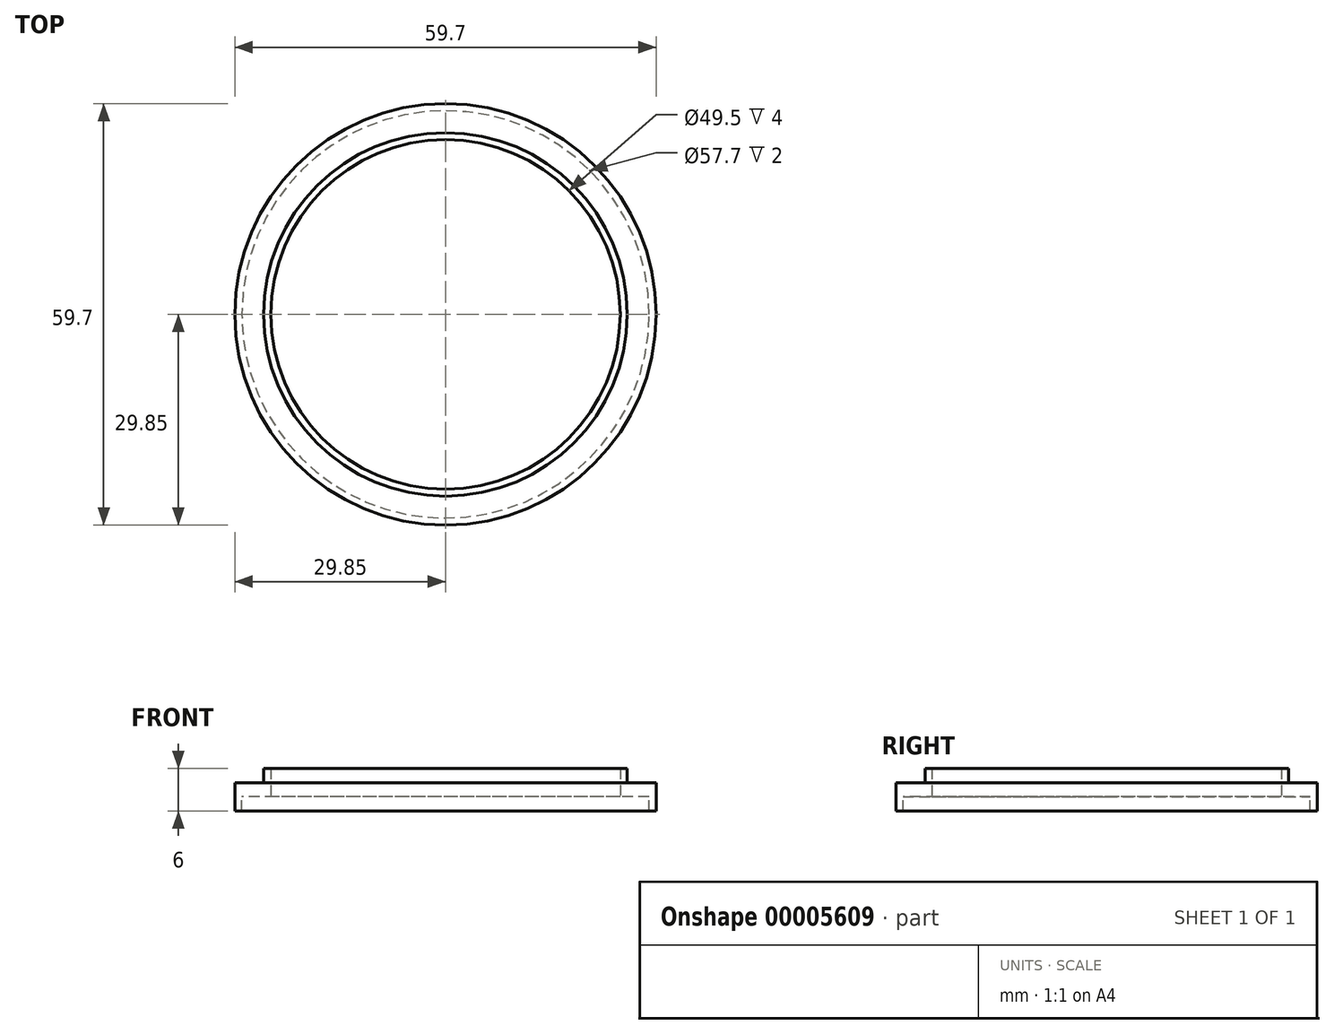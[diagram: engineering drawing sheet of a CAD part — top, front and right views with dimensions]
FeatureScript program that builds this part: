
annotation { "Feature Type Name" : "Feature", "Feature Type Description" : "" }
export const myFeature = defineFeature(function(context is Context, id is Id, definition is map)
    precondition{}
    {
        {
            var Q0;
            Q0=qCreatedBy(makeId("Top.planeOp"),FACE);
            var sketch = newSketch(context, id + "F0", { "sketchPlane" : qUnion([Q0])});
            skCircle(sketch, "E0", {"center": v(0, 0) * mm, "radius": 25.75 * mm});
            skCircle(sketch, "E1", {"center": v(0, 0) * mm, "radius": 28.85 * mm});
            skCircle(sketch, "E2.0", {"center": v(0, 0) * mm, "radius": 29.85 * mm});
            skCircle(sketch, "E3.0", {"center": v(0, 0) * mm, "radius": 24.75 * mm});
            skSolve(sketch);
        }
        {
            var Q0;
            Q0=makeQuery(id+"F0.imprint","IMPRINT",FACE,{"disambiguationData":[TD([[makeQuery(id+"F0.imprint","IMPRINT",EDGE,{"derivedFrom":sQuery(id+"F0.wireOp",EDGE,"E0")}),1.0]])]});
            var Q1;
            Q1=makeQuery(id+"F0.imprint","IMPRINT",FACE,{"disambiguationData":[TD([[makeQuery(id+"F0.imprint","IMPRINT",EDGE,{"derivedFrom":sQuery(id+"F0.wireOp",EDGE,"E1")}),-1.0]])]});
            var Q2;
            Q2=makeQuery(id+"F0.imprint","IMPRINT",FACE,{"disambiguationData":[TD([[makeQuery(id+"F0.imprint","IMPRINT",EDGE,{"derivedFrom":sQuery(id+"F0.wireOp",EDGE,"E0")}),-1.0]])]});
            extrude(context, id + "F1", {"entities" : qUnion([Q0, Q1, Q2]), "depth" : 1 * mm});
        }
        {
            var Q0;
            Q0=makeQuery(id+"F0.imprint","IMPRINT",FACE,{"disambiguationData":[TD([[makeQuery(id+"F0.imprint","IMPRINT",EDGE,{"derivedFrom":sQuery(id+"F0.wireOp",EDGE,"E0")}),1.0]])]});
            extrude(context, id + "F2", {"entities" : qUnion([Q0]), "operationType" : NewBodyOperationType.ADD, "depth" : 3 * mm});
        }
        {
            var Q0;
            Q0=makeQuery(id+"F0.imprint","IMPRINT",FACE,{"disambiguationData":[TD([[makeQuery(id+"F0.imprint","IMPRINT",EDGE,{"derivedFrom":sQuery(id+"F0.wireOp",EDGE,"E1")}),-1.0]])]});
            var Q1;
            Q1=makeQuery(id+"F0.imprint","IMPRINT",FACE,{"disambiguationData":[TD([[makeQuery(id+"F0.imprint","IMPRINT",EDGE,{"derivedFrom":sQuery(id+"F0.wireOp",EDGE,"E0")}),-1.0]])]});
            var Q2;
            Q2=makeQuery(id+"F0.imprint","IMPRINT",FACE,{"disambiguationData":[TD([[makeQuery(id+"F0.imprint","IMPRINT",EDGE,{"derivedFrom":sQuery(id+"F0.wireOp",EDGE,"E0")}),1.0]])]});
            extrude(context, id + "F3", {"entities" : qUnion([Q0, Q1, Q2]), "oppositeDirection" : true, "depth" : 1 * mm});
        }
        {
            var Q0;
            Q0=makeQuery(id+"F0.imprint","IMPRINT",FACE,{"disambiguationData":[TD([[makeQuery(id+"F0.imprint","IMPRINT",EDGE,{"derivedFrom":sQuery(id+"F0.wireOp",EDGE,"E1")}),-1.0]])]});
            extrude(context, id + "F4", {"entities" : qUnion([Q0]), "operationType" : NewBodyOperationType.ADD, "oppositeDirection" : true, "depth" : 3 * mm});
        }
    });
